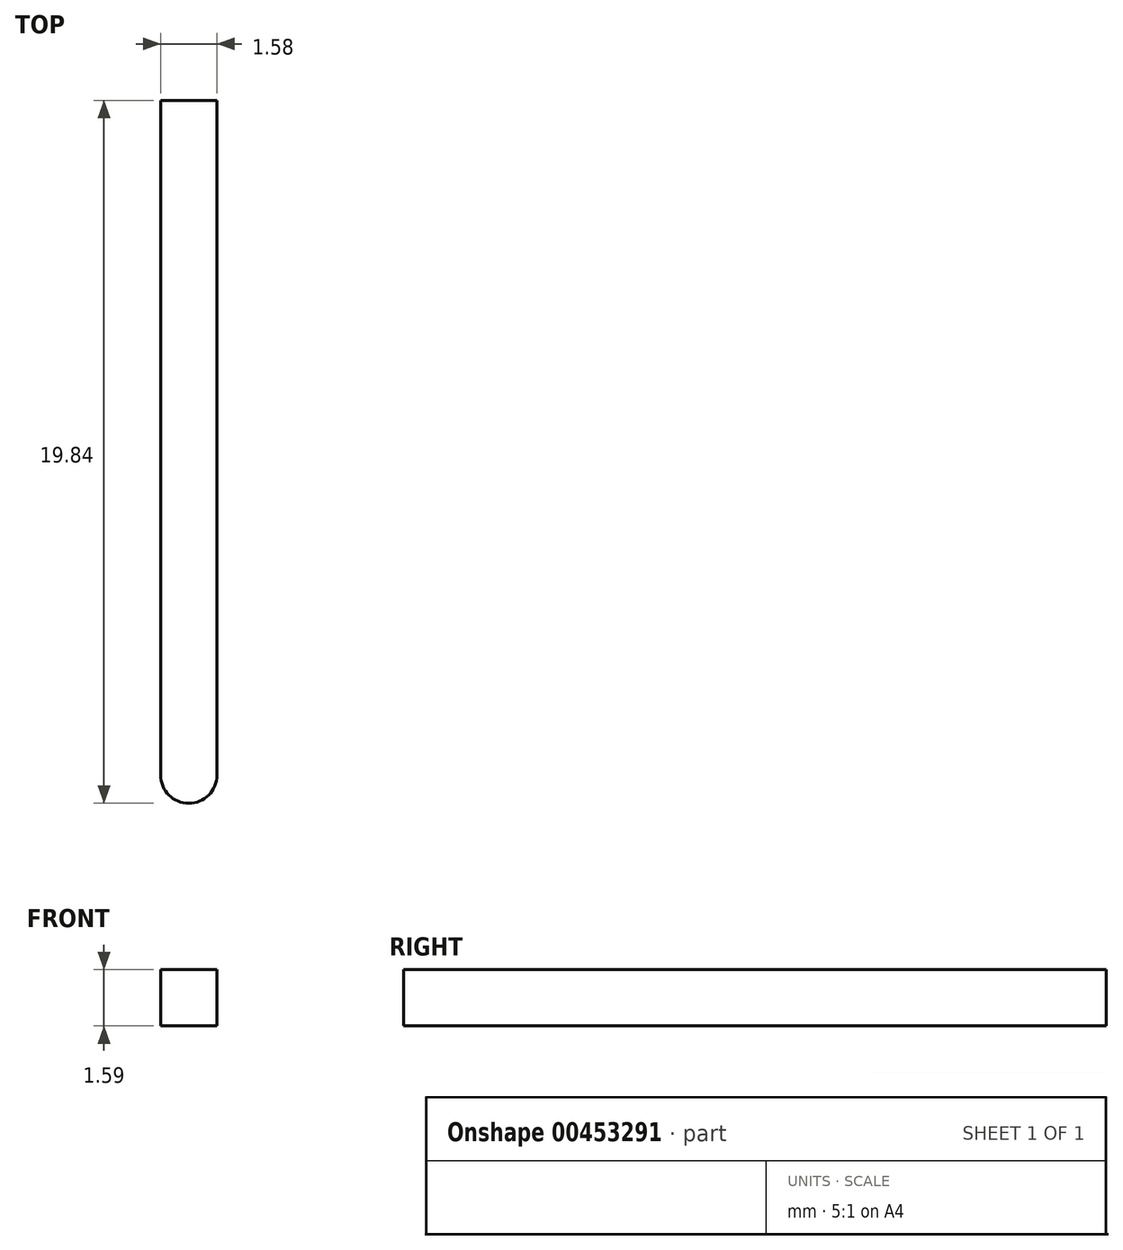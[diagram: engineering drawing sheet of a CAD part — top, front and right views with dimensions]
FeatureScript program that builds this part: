
annotation { "Feature Type Name" : "Feature", "Feature Type Description" : "" }
export const myFeature = defineFeature(function(context is Context, id is Id, definition is map)
    precondition{}
    {
        {
            var Q0;
            Q0=qCreatedBy(makeId("Top.planeOp"),FACE);
            var sketch = newSketch(context, id + "F0", { "sketchPlane" : qUnion([Q0])});
            skLineSegment(sketch, "E0.bottom", {"start": v(-127, 31.75) * mm, "end": v(127, 31.75) * mm});
            skLineSegment(sketch, "E0.top", {"start": v(-127, -31.75) * mm, "end": v(127, -31.75) * mm});
            skLineSegment(sketch, "E0.left", {"start": v(-127, 31.75) * mm, "end": v(-127, -31.75) * mm});
            skLineSegment(sketch, "E0.right", {"start": v(127, 31.75) * mm, "end": v(127, -31.75) * mm});
            skLineSegment(sketch, "E1", {"start": v(-63.5, 31.75) * mm, "end": v(-63.5, -31.75) * mm, "construction": true});
            skLineSegment(sketch, "E2", {"start": v(0, 31.75) * mm, "end": v(0, -31.75) * mm, "construction": true});
            skLineSegment(sketch, "E3", {"start": v(63.5, 31.75) * mm, "end": v(63.5, -31.75) * mm, "construction": true});
            skLineSegment(sketch, "E4", {"start": v(-63.5, 31.75) * mm, "end": v(-63.5, 12.7) * mm});
            skArc(sketch, "E5.0.startCap", {"start": v(-64.3, 31.75) * mm, "mid": v(-63.5, 32.54) * mm, "end": v(-62.7, 31.75) * mm});
            skArc(sketch, "E5.0.endCap", {"start": v(-62.7, 12.7) * mm, "mid": v(-63.5, 11.9) * mm, "end": v(-64.3, 12.7) * mm});
            skLineSegment(sketch, "E5.0.left", {"start": v(-62.7, 31.75) * mm, "end": v(-62.7, 12.7) * mm});
            skLineSegment(sketch, "E5.0.right", {"start": v(-64.3, 31.75) * mm, "end": v(-64.3, 12.7) * mm});
            skArc(sketch, "E6.MirrorCS", {"start": v(-64.3, 12.7) * mm, "mid": v(-63.5, 11.9) * mm, "end": v(-62.7, 12.7) * mm});
            skArc(sketch, "E7.MirrorCS", {"start": v(-62.7, 31.75) * mm, "mid": v(-63.5, 32.54) * mm, "end": v(-64.3, 31.75) * mm});
            skSolve(sketch);
        }
        {
            var Q0;
            Q0=makeQuery(id+"F0.imprint","IMPRINT",FACE,{"disambiguationData":[TD([[makeQuery(id+"F0.imprint","IMPRINT",EDGE,{"derivedFrom":sQuery(id+"F0.wireOp",EDGE,"E0.bottom")}),-1.0]])]});
            extrude(context, id + "F1", {"entities" : qUnion([Q0]), "depth" : 1.59 * mm});
        }
    });
